# Revit family: CADS_Vent-Axia_MechEquip_Fan_ESC_1Ph4P - SUPPLY
name_source: partatom
category: Mechanical Equipment
units: mm (PartAtom-declared; Revit-internal decimal feet)

## family parameters
Always vertical = Yes
Cut with Voids When Loaded = No
OmniClass Number = 23.75.00.00
OmniClass Title = Climate Control (HVAC)
Part Type = Normal
Room Calculation Point = No
Round Connector Dimension = Use Diameter
Shared = No
Work Plane-Based = No

## types (10) — shared parameters
AirflowRateRange = 0.0 L/s
AssemblyPlace = UNKNOWN
AssetType = FIXED
DurationUnit = Year
ExteriorInsulation = No
Fitting Type = Ignore
GrossWeight = 0.00 kg
HasProtectiveEarth = No
IfcExportAs = IfcFanType
IsExtendedWarranty = No
ManufacturerAddress = Fleming Way
Crawley 
RH10 9YX
Quantity = 1
RatedCurrent = 0 A
RatedVoltage = 0 V
Status = New
WarrantyGuarantor = Vent-Axia Limited
WorkingPressure = 0.0 Pa
zero-valued in all types: CADS_Index, CADS_Usage, Default Elevation, ExpectedServiceLife, NumberOfPoles

## per-type parameters (varying)
| type | ModelReference | NominalDiameter | NominalHeight | NominalLength | NominalWidth |
| ESC25014 | SHORT CASED AXIAL FAN 250DIA 1PH 4 POLE | 250 mm  [stored 0.82021 ft] | 250 mm  [stored 0.82021 ft] | 110 mm  [stored 0.360892 ft] | 250 mm  [stored 0.82021 ft] |
| ESC31514 | SHORT CASED AXIAL FAN 315DIA 1PH 4 POLE | 315 mm  [stored 1.03346 ft] | 315 mm  [stored 1.03346 ft] | 135 mm  [stored 0.442913 ft] | 315 mm  [stored 1.03346 ft] |
| ESC35514 | SHORT CASED AXIAL FAN 355DIA 1PH 4 POLE | 355 mm | 355 mm | 135 mm  [stored 0.442913 ft] | 355 mm |
| ESC35514B | 355MM 1PH 4P CASED FAN FC035-4EF.2C.A7 169567 | 355 mm | 355 mm | 135 mm  [stored 0.442913 ft] | 355 mm |
| ESC40014 | SHORT CASED AXIAL FAN 400DIA 1PH 4 POLE | 400 mm  [stored 1.31234 ft] | 400 mm  [stored 1.31234 ft] | 155 mm  [stored 0.50853 ft] | 400 mm  [stored 1.31234 ft] |
| ESC40014B | 400MM 1PH 4P CASED FAN FC040-4EF.2F.A7 169493 | 400 mm  [stored 1.31234 ft] | 400 mm  [stored 1.31234 ft] | 155 mm  [stored 0.50853 ft] | 400 mm  [stored 1.31234 ft] |
| ESC45014 | SHORT CASED AXIAL FAN 450DIA 1PH 4 POLE | 450 mm  [stored 1.47638 ft] | 450 mm  [stored 1.47638 ft] | 160 mm  [stored 0.524934 ft] | 450 mm  [stored 1.47638 ft] |
| ESC50014 | SHORT CASED AXIAL FAN 500DIA 1PH 4 POLE | 500 mm  [stored 1.64042 ft] | 500 mm  [stored 1.64042 ft] | 166 mm  [stored 0.544619 ft] | 500 mm  [stored 1.64042 ft] |
| ESC56014C | 560MM 1PH 4P CASED FAN ART. 183562 | 560 mm  [stored 1.83727 ft] | 560 mm  [stored 1.83727 ft] | 210 mm  [stored 0.688976 ft] | 560 mm  [stored 1.83727 ft] |
| ESC63014 | SHORT CASED AXIAL FAN 630DIA 1PH 4 POLE | 630 mm  [stored 2.06693 ft] | 630 mm  [stored 2.06693 ft] | 220 mm  [stored 0.721785 ft] | 630 mm  [stored 2.06693 ft] |

note: column(s) folded — value = type name in every type: ModelNumber

note: [stored X ft] marks values corroborated as IEEE doubles in the binary element streams (Revit-internal decimal feet)

## geometry (parser evidence)
native form markers: Sweep x10
no freeform markers — native parametric forms only
